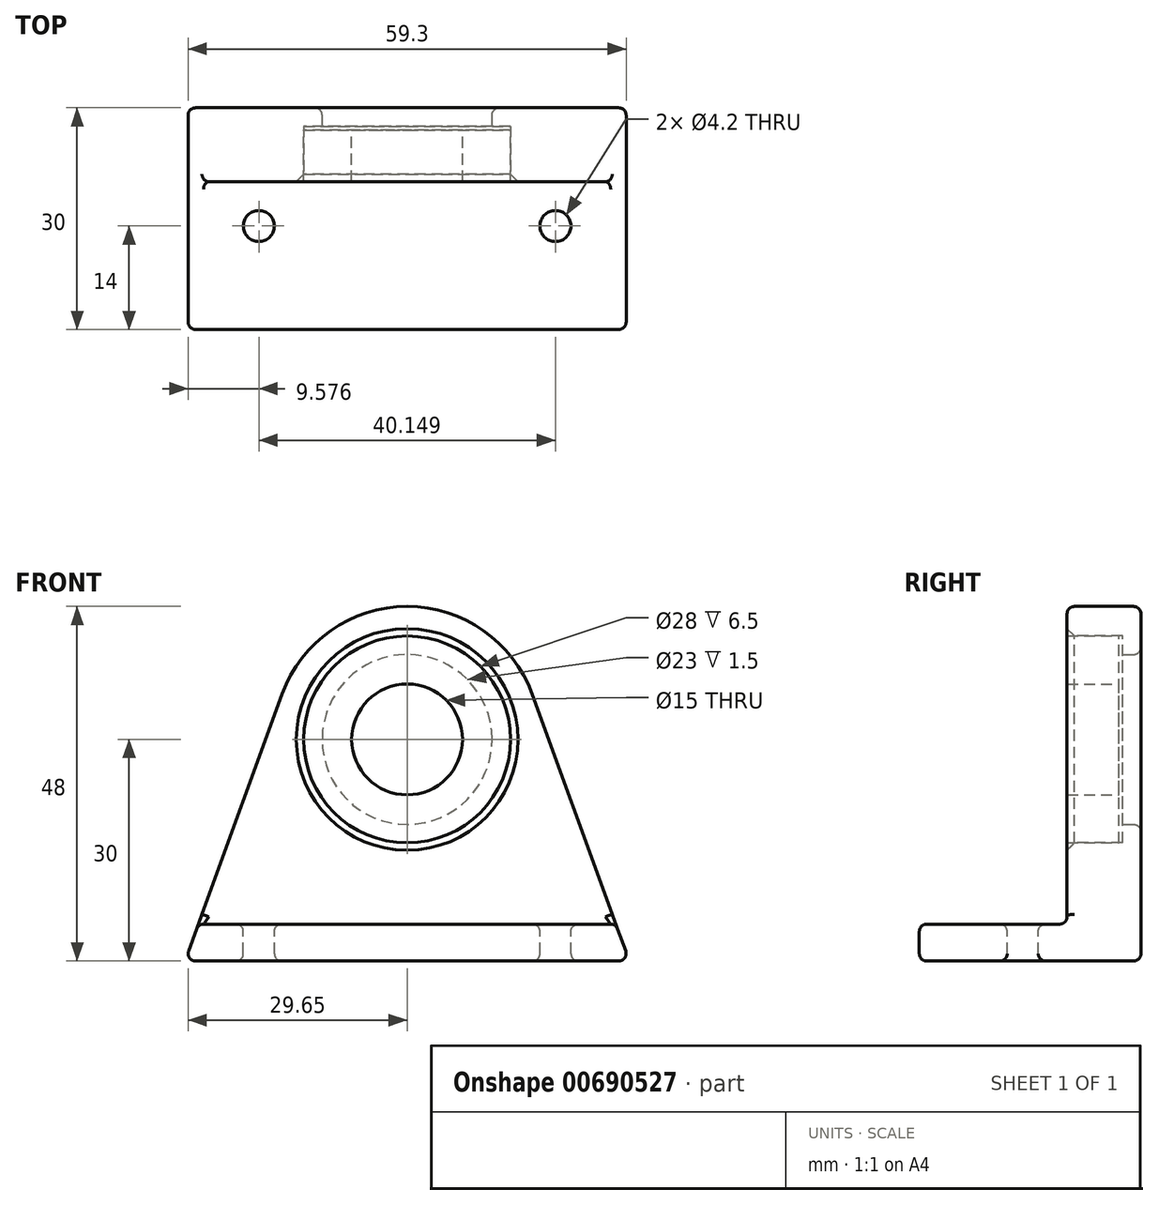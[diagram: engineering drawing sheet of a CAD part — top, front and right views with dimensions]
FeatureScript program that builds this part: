
annotation { "Feature Type Name" : "Feature", "Feature Type Description" : "" }
export const myFeature = defineFeature(function(context is Context, id is Id, definition is map)
    precondition{}
    {
        {
            var Q0;
            Q0=qCreatedBy(makeId("Front.planeOp"),FACE);
            var sketch = newSketch(context, id + "F0", { "sketchPlane" : qUnion([Q0])});
            skCircle(sketch, "E0", {"center": v(0, 0) * mm, "radius": 7.5 * mm});
            skCircle(sketch, "E1", {"center": v(0, 0) * mm, "radius": 14 * mm});
            skSolve(sketch);
        }
        {
            var Q0;
            Q0=makeQuery(id+"F0.imprint","IMPRINT",FACE,{"disambiguationData":[TD([[makeQuery(id+"F0.imprint","IMPRINT",EDGE,{"derivedFrom":sQuery(id+"F0.wireOp",EDGE,"E0")}),-1.0]])]});
            extrude(context, id + "F1", {"entities" : qUnion([Q0]), "depth" : 7 * mm, "offsetDistance" : 25 * mm});
        }
        {
            var Q0;
            Q0=makeQuery(id+"F1.opExtrude","CAP_FACE",FACE,{"disambiguationData":[OSD([sQuery(id+"F0.wireOp",EDGE,"E0"),sQuery(id+"F0.wireOp",EDGE,"E1")])],"isStart":false});
            var sketch = newSketch(context, id + "F2", { "sketchPlane" : qUnion([Q0])});
            skCircle(sketch, "E2", {"center": v(0, 0) * mm, "radius": 18 * mm});
            skLineSegment(sketch, "E3", {"start": v(-30.07, -30) * mm, "end": v(30.07, -30) * mm});
            skLineSegment(sketch, "E4", {"start": v(-30.07, -30) * mm, "end": v(-16.91, 6.16) * mm});
            skLineSegment(sketch, "E5", {"start": v(16.91, 6.16) * mm, "end": v(30.07, -30) * mm});
            skSolve(sketch);
        }
        {
            var Q0;
            Q0=makeQuery(id+"F2.imprint","IMPRINT",FACE,{"disambiguationData":[TD([[makeQuery(id+"F2.imprint","IMPRINT",EDGE,{"derivedFrom":sQuery(id+"F2.wireOp",EDGE,"E3")}),1.0]])]});
            var Q1;
            Q1=makeQuery(id+"F2.imprint","IMPRINT",FACE,{"disambiguationData":[TD([[makeQuery(id+"F2.imprint","IMPRINT",EDGE,{"derivedFrom":makeQuery(id+"F1.opExtrude","CAP_EDGE",EDGE,{"disambiguationData":[OSD([sQuery(id+"F0.wireOp",EDGE,"E1")])],"isStart":false})}),-1.0]])]});
            extrude(context, id + "F3", {"entities" : qUnion([Q0, Q1]), "oppositeDirection" : true, "depth" : (7 + 3) * mm, "offsetDistance" : 25 * mm});
        }
        {
            var Q0;
            Q0=makeQuery(id+"F3.opExtrude","CAP_FACE",FACE,{"disambiguationData":[OSD([sQuery(id+"F0.wireOp",EDGE,"E1"),sQuery(id+"F2.wireOp",EDGE,"E2"),sQuery(id+"F2.wireOp",EDGE,"E3"),sQuery(id+"F2.wireOp",EDGE,"E4"),sQuery(id+"F2.wireOp",EDGE,"E5")])],"isStart":false});
            var sketch = newSketch(context, id + "F4", { "sketchPlane" : qUnion([Q0])});
            skCircle(sketch, "E6", {"center": v(0, 0) * mm, "radius": 14 * mm});
            skCircle(sketch, "E7", {"center": v(0, 0) * mm, "radius": 11.5 * mm});
            skSolve(sketch);
        }
        {
            var Q0;
            Q0=makeQuery(id+"F4.imprint","IMPRINT",FACE,{"disambiguationData":[TD([[makeQuery(id+"F4.imprint","IMPRINT",EDGE,{"derivedFrom":sQuery(id+"F4.wireOp",EDGE,"E6")}),-1.0]])]});
            var Q1;
            Q1=makeQuery(id+"F1.opExtrude","CAP_FACE",FACE,{"disambiguationData":[OSD([sQuery(id+"F0.wireOp",EDGE,"E0"),sQuery(id+"F0.wireOp",EDGE,"E1")])],"isStart":true});
            extrude(context, id + "F5", {"entities" : qUnion([Q0]), "operationType" : NewBodyOperationType.ADD, "endBound" : BoundingType.UP_TO_SURFACE, "oppositeDirection" : true, "depth" : 25 * mm, "endBoundEntityFace" : qUnion([Q1]), "hasOffset" : true, "offsetDistance" : 0.5 * mm});
        }
        {
            var Q0;
            Q0=makeQuery(id+"F3.opExtrude","CAP_FACE",FACE,{"disambiguationData":[OSD([sQuery(id+"F0.wireOp",EDGE,"E1"),sQuery(id+"F2.wireOp",EDGE,"E2"),sQuery(id+"F2.wireOp",EDGE,"E3"),sQuery(id+"F2.wireOp",EDGE,"E4"),sQuery(id+"F2.wireOp",EDGE,"E5")])],"isStart":true});
            var sketch = newSketch(context, id + "F6", { "sketchPlane" : qUnion([Q0])});
            skLineSegment(sketch, "E8", {"start": v(-30.07, -30) * mm, "end": v(30.07, -30) * mm});
            skLineSegment(sketch, "E9", {"start": v(30.07, -30) * mm, "end": v(28.25, -25) * mm});
            skLineSegment(sketch, "E10", {"start": v(28.25, -25) * mm, "end": v(-28.25, -25) * mm});
            skLineSegment(sketch, "E11", {"start": v(-28.25, -25) * mm, "end": v(-30.07, -30) * mm});
            skSolve(sketch);
        }
        {
            var Q0;
            Q0 = qSketchRegion(id + "F6", true);
            extrude(context, id + "F7", {"entities" : qUnion([Q0]), "operationType" : NewBodyOperationType.ADD, "depth" : 20 * mm, "offsetDistance" : 25 * mm});
        }
        {
            var Q0;
            Q0=makeQuery(id+"F7.opExtrude","SWEPT_FACE",FACE,{"disambiguationData":[OSD([sQuery(id+"F6.wireOp",EDGE,"E10")])]});
            var sketch = newSketch(context, id + "F8", { "sketchPlane" : qUnion([Q0])});
            skCircle(sketch, "E12", {"center": v(-20.07, -13) * mm, "radius": 2.1 * mm});
            skCircle(sketch, "E13", {"center": v(20.07, -13) * mm, "radius": 2.1 * mm});
            skSolve(sketch);
        }
        {
            var Q0;
            Q0=makeQuery(id+"F8.imprint","IMPRINT",FACE,{"disambiguationData":[TD([[makeQuery(id+"F8.imprint","IMPRINT",EDGE,{"derivedFrom":sQuery(id+"F8.wireOp",EDGE,"E12")}),1.0]])]});
            var Q1;
            Q1=makeQuery(id+"F8.imprint","IMPRINT",FACE,{"disambiguationData":[TD([[makeQuery(id+"F8.imprint","IMPRINT",EDGE,{"derivedFrom":sQuery(id+"F8.wireOp",EDGE,"E13")}),1.0]])]});
            extrude(context, id + "F9", {"entities" : qUnion([Q0, Q1]), "operationType" : NewBodyOperationType.REMOVE, "oppositeDirection" : true, "depth" : 25 * mm, "offsetDistance" : 25 * mm});
        }
        {
            var Q0;
            Q0=makeQuery(id+"F7.boolean.opBoolean","MERGE",FACE,{"derivedFrom":[makeQuery(id+"F3.opExtrude","SWEPT_FACE",FACE,{"disambiguationData":[OSD([sQuery(id+"F2.wireOp",EDGE,"E4")])]}),makeQuery(id+"F7.opExtrude","SWEPT_FACE",FACE,{"disambiguationData":[OSD([sQuery(id+"F6.wireOp",EDGE,"E11")])]})]});
            var Q1;
            Q1=makeQuery(id+"F3.opExtrude","SWEPT_FACE",FACE,{"disambiguationData":[OSD([sQuery(id+"F2.wireOp",EDGE,"E2")])]});
            var Q2;
            Q2=makeQuery(id+"F7.boolean.opBoolean","MERGE",FACE,{"derivedFrom":[makeQuery(id+"F3.opExtrude","SWEPT_FACE",FACE,{"disambiguationData":[OSD([sQuery(id+"F2.wireOp",EDGE,"E5")])]}),makeQuery(id+"F7.opExtrude","SWEPT_FACE",FACE,{"disambiguationData":[OSD([sQuery(id+"F6.wireOp",EDGE,"E9")])]})]});
            var Q3;
            Q3=makeQuery(id+"F7.opExtrude","SWEPT_FACE",FACE,{"disambiguationData":[OSD([sQuery(id+"F6.wireOp",EDGE,"E10")])]});
            var Q4;
            Q4=makeQuery(id+"F7.opExtrude","CAP_FACE",FACE,{"disambiguationData":[OSD([sQuery(id+"F6.wireOp",EDGE,"E8"),sQuery(id+"F6.wireOp",EDGE,"E9"),sQuery(id+"F6.wireOp",EDGE,"E10"),sQuery(id+"F6.wireOp",EDGE,"E11")])],"isStart":false});
            var Q5;
            Q5=makeQuery(id+"F7.boolean.opBoolean","MERGE",FACE,{"derivedFrom":[makeQuery(id+"F3.opExtrude","SWEPT_FACE",FACE,{"disambiguationData":[OSD([sQuery(id+"F2.wireOp",EDGE,"E3")])]}),makeQuery(id+"F7.opExtrude","SWEPT_FACE",FACE,{"disambiguationData":[OSD([sQuery(id+"F6.wireOp",EDGE,"E8")])]})]});
            var Q6;
            Q6=makeQuery(id+"F5.boolean.opBoolean","MERGE",FACE,{"derivedFrom":[makeQuery(id+"F3.opExtrude","CAP_FACE",FACE,{"disambiguationData":[OSD([sQuery(id+"F0.wireOp",EDGE,"E1"),sQuery(id+"F2.wireOp",EDGE,"E2"),sQuery(id+"F2.wireOp",EDGE,"E3"),sQuery(id+"F2.wireOp",EDGE,"E4"),sQuery(id+"F2.wireOp",EDGE,"E5")])],"isStart":false}),makeQuery(id+"F5.opExtrude","CAP_FACE",FACE,{"disambiguationData":[OSD([sQuery(id+"F4.wireOp",EDGE,"E6"),sQuery(id+"F4.wireOp",EDGE,"E7")])],"isStart":true})]});
            fillet(context, id + "F10", {"entities" : qUnion([Q0, Q1, Q2, Q3, Q4, Q5, Q6]), "radius" : 1 * mm, "tangentPropagation" : true, "allowEdgeOverflow" : false});
        }
        {
            var Q0;
            Q0=makeQuery(id+"F3.opExtrude","CAP_EDGE",EDGE,{"disambiguationData":[OSD([sQuery(id+"F0.wireOp",EDGE,"E1")])],"isStart":true});
            chamfer(context, id + "F11", {"entities" : qUnion([Q0]), "width" : 1 * mm, "tangentPropagation" : true});
        }
    });
